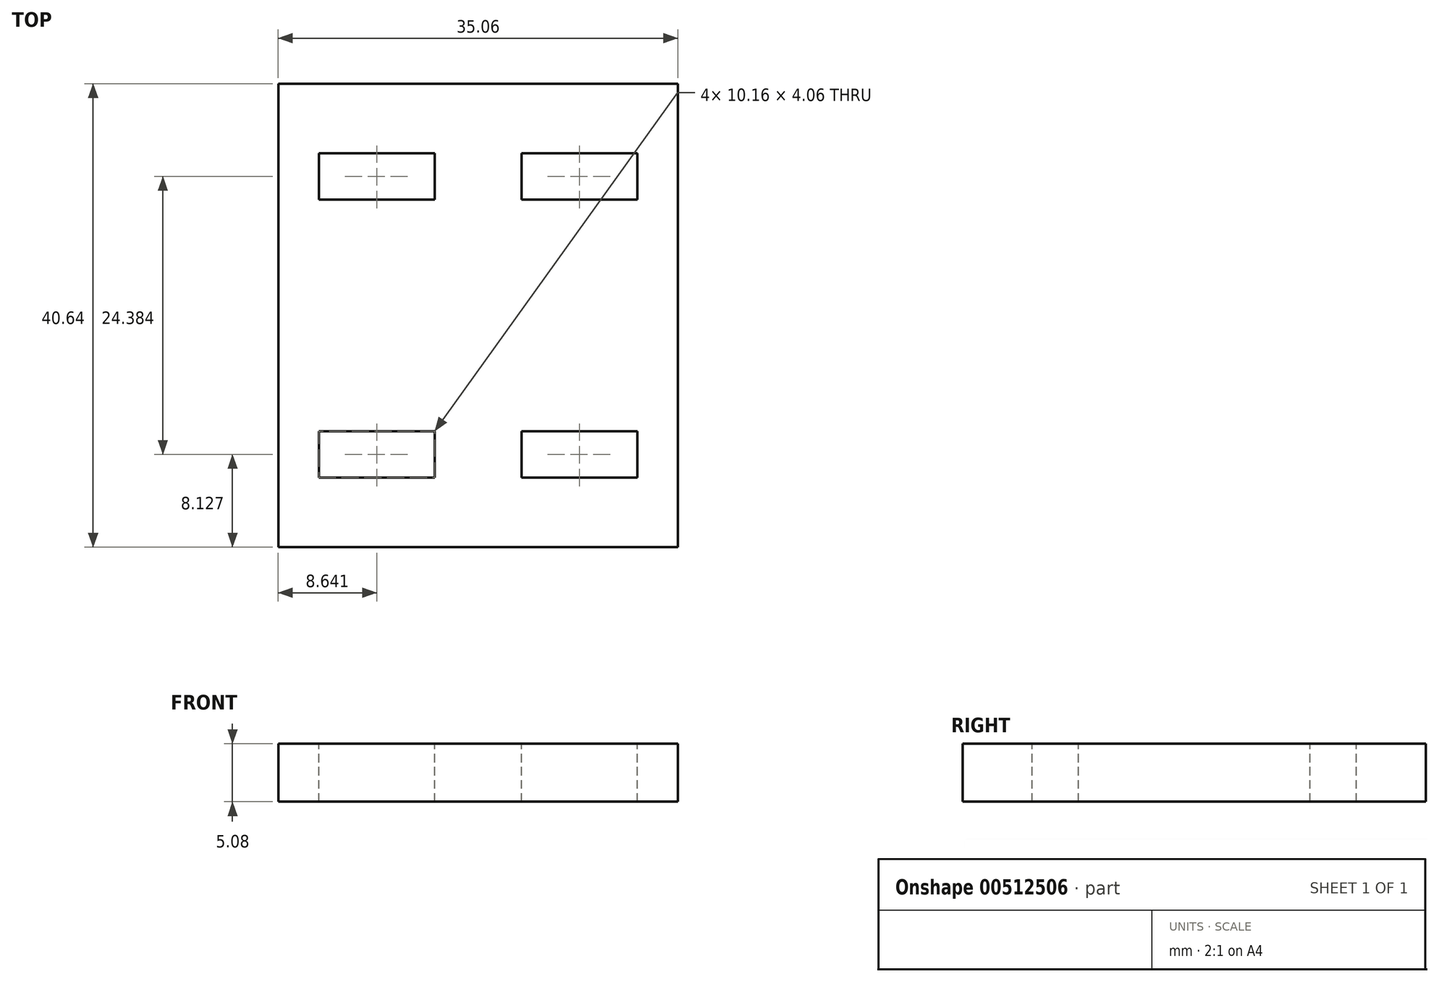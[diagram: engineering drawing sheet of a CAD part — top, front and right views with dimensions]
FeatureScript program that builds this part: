
annotation { "Feature Type Name" : "Feature", "Feature Type Description" : "" }
export const myFeature = defineFeature(function(context is Context, id is Id, definition is map)
    precondition{}
    {
        {
            var Q0;
            Q0=qCreatedBy(makeId("Top.planeOp"),FACE);
            var sketch = newSketch(context, id + "F0", { "sketchPlane" : qUnion([Q0])});
            skLineSegment(sketch, "E0.bottom", {"start": v(-37.06, -28.6) * mm, "end": v(-2, -28.6) * mm});
            skLineSegment(sketch, "E0.top", {"start": v(-37.06, 12.05) * mm, "end": v(-2, 12.05) * mm});
            skLineSegment(sketch, "E0.left", {"start": v(-37.06, -28.6) * mm, "end": v(-37.06, 12.05) * mm});
            skLineSegment(sketch, "E0.right", {"start": v(-2, -28.6) * mm, "end": v(-2, 12.05) * mm});
            skSolve(sketch);
        }
        {
            var Q0;
            Q0=makeQuery(id+"F0.imprint","IMPRINT",FACE,{"disambiguationData":[TD([[makeQuery(id+"F0.imprint","IMPRINT",EDGE,{"derivedFrom":sQuery(id+"F0.wireOp",EDGE,"E0.bottom")}),1.0]])]});
            extrude(context, id + "F1", {"entities" : qUnion([Q0]), "depth" : 5.08 * mm});
        }
        {
            var Q0;
            Q0=makeQuery(id+"F1.opExtrude","CAP_FACE",FACE,{"disambiguationData":[OSD([sQuery(id+"F0.wireOp",EDGE,"E0.bottom"),sQuery(id+"F0.wireOp",EDGE,"E0.top"),sQuery(id+"F0.wireOp",EDGE,"E0.left"),sQuery(id+"F0.wireOp",EDGE,"E0.right")])],"isStart":false});
            var sketch = newSketch(context, id + "F2", { "sketchPlane" : qUnion([Q0])});
            skLineSegment(sketch, "E1.bottom", {"start": v(-33.5, 1.89) * mm, "end": v(-23.34, 1.89) * mm});
            skLineSegment(sketch, "E1.top", {"start": v(-33.5, 5.95) * mm, "end": v(-23.34, 5.95) * mm});
            skLineSegment(sketch, "E1.left", {"start": v(-33.5, 5.95) * mm, "end": v(-33.5, 1.89) * mm});
            skLineSegment(sketch, "E1.right", {"start": v(-23.34, 5.95) * mm, "end": v(-23.34, 1.89) * mm});
            skLineSegment(sketch, "E2.bottom", {"start": v(-15.72, 1.89) * mm, "end": v(-5.56, 1.89) * mm});
            skLineSegment(sketch, "E2.top", {"start": v(-15.72, 5.95) * mm, "end": v(-5.56, 5.95) * mm});
            skLineSegment(sketch, "E2.left", {"start": v(-15.72, 5.95) * mm, "end": v(-15.72, 1.89) * mm});
            skLineSegment(sketch, "E2.right", {"start": v(-5.56, 5.95) * mm, "end": v(-5.56, 1.89) * mm});
            skLineSegment(sketch, "E3.bottom", {"start": v(-33.5, -18.43) * mm, "end": v(-23.34, -18.43) * mm});
            skLineSegment(sketch, "E3.top", {"start": v(-33.5, -22.5) * mm, "end": v(-23.34, -22.5) * mm});
            skLineSegment(sketch, "E3.left", {"start": v(-33.5, -18.43) * mm, "end": v(-33.5, -22.5) * mm});
            skLineSegment(sketch, "E3.right", {"start": v(-23.34, -18.43) * mm, "end": v(-23.34, -22.5) * mm});
            skLineSegment(sketch, "E4.bottom", {"start": v(-15.72, -18.43) * mm, "end": v(-5.56, -18.43) * mm});
            skLineSegment(sketch, "E4.top", {"start": v(-15.72, -22.5) * mm, "end": v(-5.56, -22.5) * mm});
            skLineSegment(sketch, "E4.left", {"start": v(-15.72, -18.43) * mm, "end": v(-15.72, -22.5) * mm});
            skLineSegment(sketch, "E4.right", {"start": v(-5.56, -18.43) * mm, "end": v(-5.56, -22.5) * mm});
            skLineSegment(sketch, "E5", {"start": v(-37.06, -8.27) * mm, "end": v(-2, -8.27) * mm, "construction": true});
            skLineSegment(sketch, "E6", {"start": v(-19.53, -28.6) * mm, "end": v(-19.53, 12.05) * mm, "construction": true});
            skSolve(sketch);
        }
        {
            var Q0;
            Q0=makeQuery(id+"F2.imprint","IMPRINT",FACE,{"disambiguationData":[TD([[makeQuery(id+"F2.imprint","IMPRINT",EDGE,{"derivedFrom":sQuery(id+"F2.wireOp",EDGE,"E1.bottom")}),1.0]])]});
            var Q1;
            Q1=makeQuery(id+"F2.imprint","IMPRINT",FACE,{"disambiguationData":[TD([[makeQuery(id+"F2.imprint","IMPRINT",EDGE,{"derivedFrom":sQuery(id+"F2.wireOp",EDGE,"E2.bottom")}),1.0]])]});
            var Q2;
            Q2=makeQuery(id+"F2.imprint","IMPRINT",FACE,{"disambiguationData":[TD([[makeQuery(id+"F2.imprint","IMPRINT",EDGE,{"derivedFrom":sQuery(id+"F2.wireOp",EDGE,"E4.bottom")}),-1.0]])]});
            var Q3;
            Q3=makeQuery(id+"F2.imprint","IMPRINT",FACE,{"disambiguationData":[TD([[makeQuery(id+"F2.imprint","IMPRINT",EDGE,{"derivedFrom":sQuery(id+"F2.wireOp",EDGE,"E3.bottom")}),-1.0]])]});
            extrude(context, id + "F3", {"entities" : qUnion([Q0, Q1, Q2, Q3]), "operationType" : NewBodyOperationType.REMOVE, "oppositeDirection" : true, "depth" : 25.4 * mm});
        }
    });
